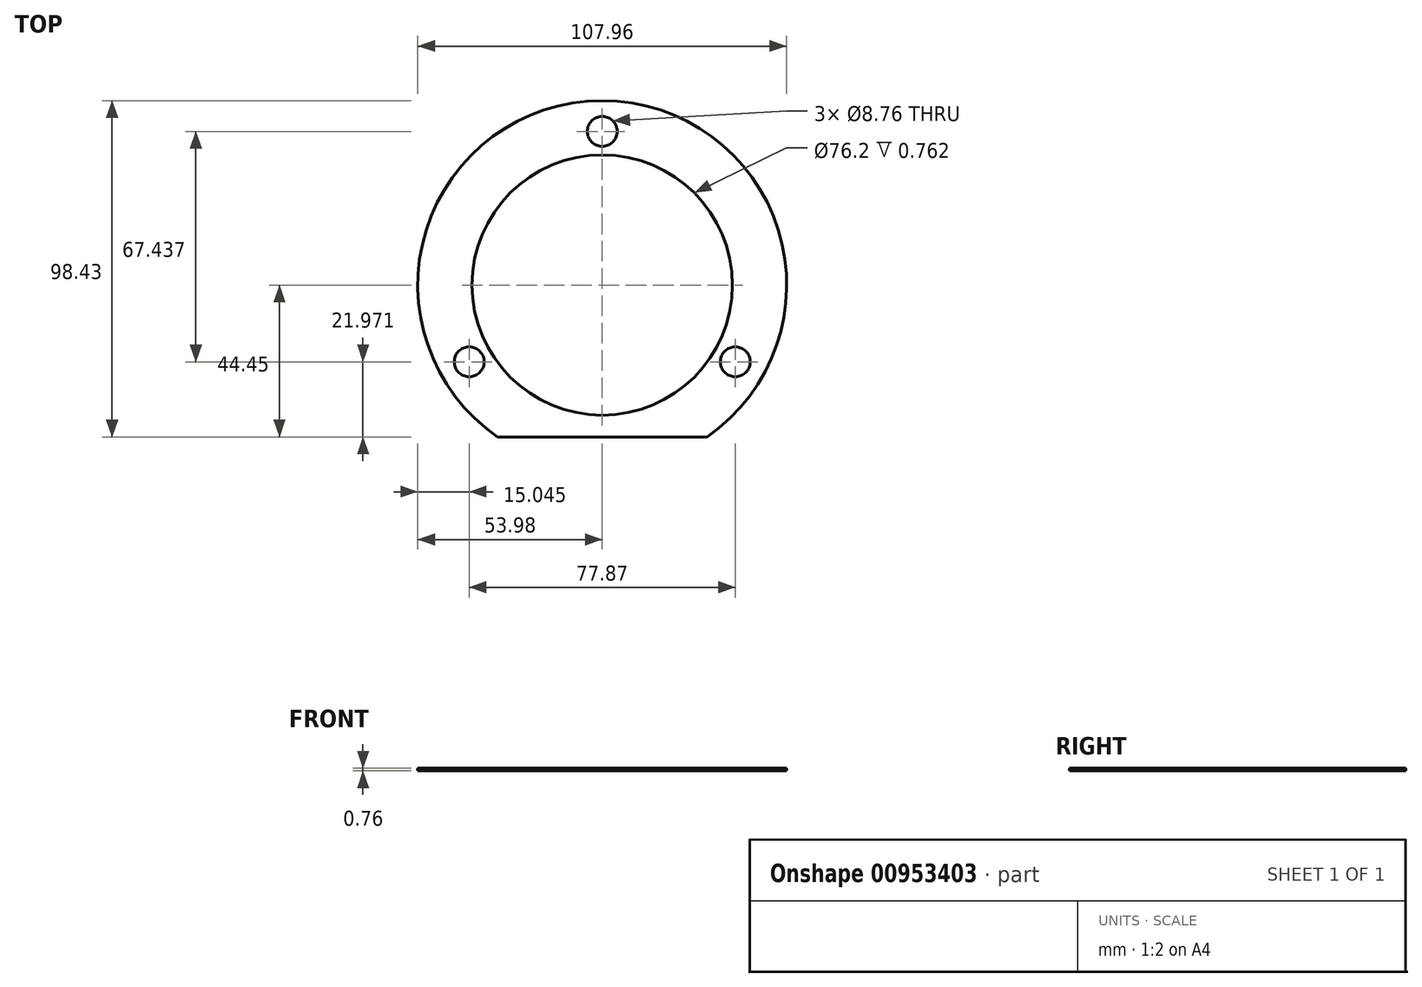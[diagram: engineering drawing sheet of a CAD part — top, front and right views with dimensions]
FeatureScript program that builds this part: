
annotation { "Feature Type Name" : "Feature", "Feature Type Description" : "" }
export const myFeature = defineFeature(function(context is Context, id is Id, definition is map)
    precondition{}
    {
        {
            var Q0;
            Q0=qCreatedBy(makeId("Top.planeOp"),FACE);
            var sketch = newSketch(context, id + "F0", { "sketchPlane" : qUnion([Q0])});
            skArc(sketch, "E0", {"start": v(30.62, -44.45) * mm, "mid": v(0, 53.98) * mm, "end": v(-30.62, -44.45) * mm});
            skCircle(sketch, "E1", {"center": v(0, 0) * mm, "radius": 38.1 * mm});
            skArc(sketch, "E2", {"start": v(6.74, -44.45) * mm, "mid": v(0, 44.96) * mm, "end": v(-6.74, -44.45) * mm, "construction": true});
            skCircle(sketch, "E3", {"center": v(0, 44.96) * mm, "radius": 4.38 * mm});
            skCircle(sketch, "E4.1.0", {"center": v(-38.93, -22.48) * mm, "radius": 4.38 * mm});
            skCircle(sketch, "E4.2.0", {"center": v(38.93, -22.48) * mm, "radius": 4.38 * mm});
            skLineSegment(sketch, "E5", {"start": v(-30.62, -44.45) * mm, "end": v(30.62, -44.45) * mm});
            skSolve(sketch);
        }
        {
            var Q0;
            Q0=makeQuery(id+"F0.imprint","IMPRINT",FACE,{"disambiguationData":[TD([[makeQuery(id+"F0.imprint","IMPRINT",EDGE,{"derivedFrom":sQuery(id+"F0.wireOp",EDGE,"E0")}),1.0]])]});
            extrude(context, id + "F1", {"entities" : qUnion([Q0]), "depth" : 0.76 * mm, "offsetDistance" : 25.4 * mm});
        }
    });
